# Revit family: Table-Teknion-CQTSB-Routes-Square_Adjustable_Side_Table-R2022
name_source: partatom
category: Furniture
units: mm (PartAtom-declared; Revit-internal decimal feet)

## family parameters
Always vertical = Yes
Cut with Voids When Loaded = No
OmniClass Number = 23.40.20.00
OmniClass Title = General Furniture and Specialties
Render Appearance Source = Family Geometry
Room Calculation Point = No
Shared = Yes
Work Plane-Based = No

## types (1)
- CQTSB16
    Assembly Code = E2020200
    Default Elevation = 0 "
    Depth = 0 "
    Description = Routes - Square Adjustable Side Table
    Frame Finish = Grade 2 Laminate - Teknion - WV - Midnight
    Height = 18 "
    Length = 0 "
    Manufacturer = Teknion
    Manufacturer Fax = 416.661.4586
    Model = CQTSB16
    Part Number = CQTSB
    Product Documentation Link = https://www.teknion.com
    Product Line = Side Table
    Product Page URL = https://www.teknion.com
    Series = Routes
    Surface Finish = Foundation Laminate-Teknion-4L-Baltic_Ply
    Sustainability Data = https://www.teknion.com
    URL = www.teknion.com
    Unit Weight URL = http://www.teknion.com
    Warranty = http://www.teknion.com
    Width = 0 "

## geometry (parser evidence)
native form markers: Sweep x3
no freeform markers — native parametric forms only
